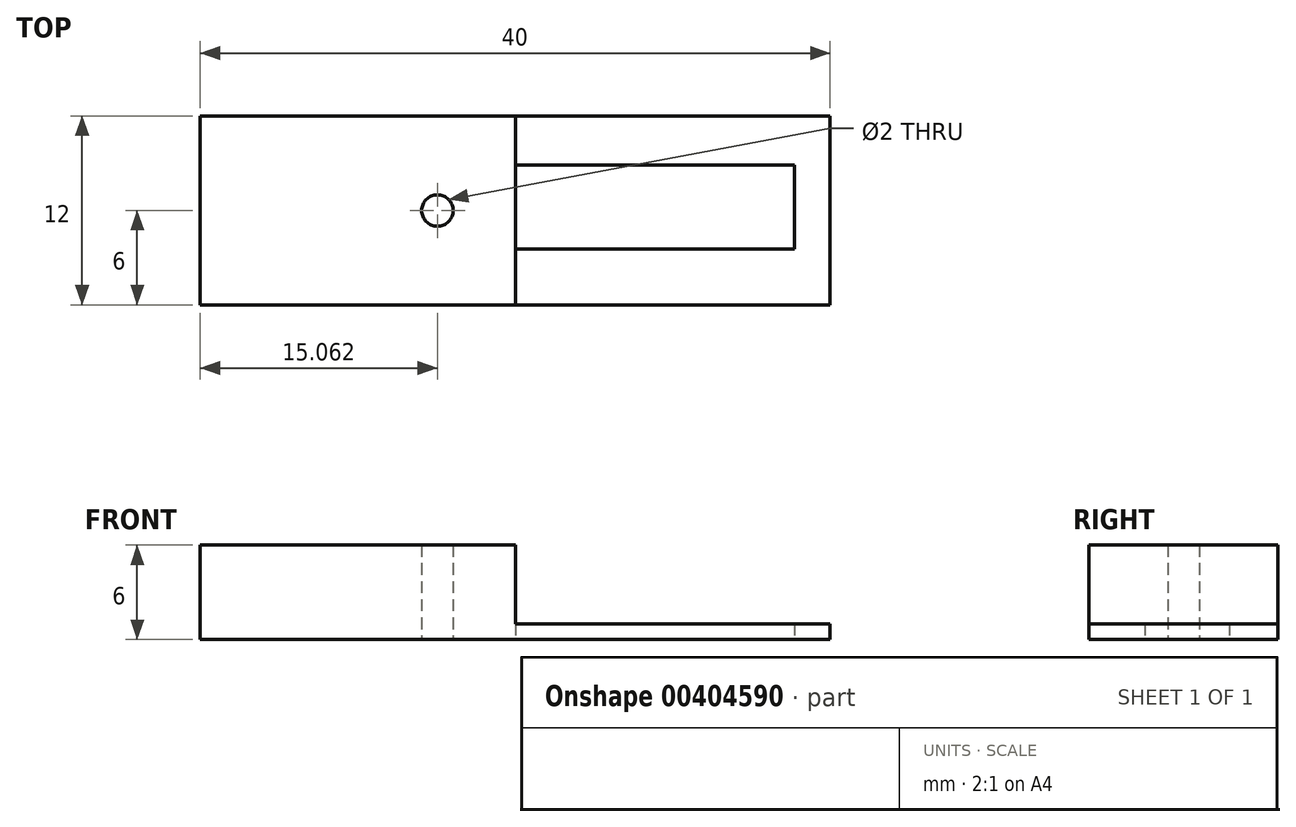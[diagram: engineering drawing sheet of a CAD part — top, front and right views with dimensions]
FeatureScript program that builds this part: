
annotation { "Feature Type Name" : "Feature", "Feature Type Description" : "" }
export const myFeature = defineFeature(function(context is Context, id is Id, definition is map)
    precondition{}
    {
        {
            var Q0;
            Q0=qCreatedBy(makeId("Top.planeOp"),FACE);
            var sketch = newSketch(context, id + "F0", { "sketchPlane" : qUnion([Q0])});
            skLineSegment(sketch, "E0.bottom", {"start": v(0, 0) * mm, "end": v(-40, 0) * mm});
            skLineSegment(sketch, "E0.top", {"start": v(0, 12) * mm, "end": v(-40, 12) * mm});
            skLineSegment(sketch, "E0.left", {"start": v(0, 0) * mm, "end": v(0, 12) * mm});
            skLineSegment(sketch, "E0.right", {"start": v(-40, 0) * mm, "end": v(-40, 12) * mm});
            skLineSegment(sketch, "E1", {"start": v(-40, 6) * mm, "end": v(-25, 6) * mm});
            skLineSegment(sketch, "E2", {"start": v(-24.94, 12) * mm, "end": v(-24.94, 6) * mm});
            skLineSegment(sketch, "E3", {"start": v(-25, 6) * mm, "end": v(-24.94, 6) * mm});
            skCircle(sketch, "E4", {"center": v(-24.94, 6) * mm, "radius": 1 * mm});
            skLineSegment(sketch, "E5", {"start": v(-40, 6) * mm, "end": v(-19.97, 6) * mm});
            skLineSegment(sketch, "E6", {"start": v(-40, 3.56) * mm, "end": v(-19.97, 3.56) * mm});
            skLineSegment(sketch, "E7.bottom", {"start": v(-19.97, 3.56) * mm, "end": v(-2.25, 3.56) * mm});
            skLineSegment(sketch, "E7.top", {"start": v(-19.97, 8.9) * mm, "end": v(-2.25, 8.9) * mm});
            skLineSegment(sketch, "E7.left", {"start": v(-19.97, 3.56) * mm, "end": v(-19.97, 8.9) * mm});
            skLineSegment(sketch, "E7.right", {"start": v(-2.25, 3.56) * mm, "end": v(-2.25, 8.9) * mm});
            skLineSegment(sketch, "E8", {"start": v(-19.97, 8.9) * mm, "end": v(-19.97, 12) * mm});
            skLineSegment(sketch, "E9", {"start": v(-19.97, 12) * mm, "end": v(-19.97, 0) * mm});
            skLineSegment(sketch, "E10", {"start": v(-24.94, 6) * mm, "end": v(-25, 0) * mm});
            skSolve(sketch);
        }
        {
            var Q0;
            {var subQ9=sQuery(id+"F0.wireOp",EDGE,"E0.bottom");Q0=makeQuery(id+"F0.imprint","IMPRINT",FACE,{"disambiguationData":[TD([[makeQuery(id+"F0.imprint","IMPRINT",EDGE,{"derivedFrom":subQ9}),-1.0]])]});}
            var Q1;
            {var subQ8=sQuery(id+"F0.wireOp",EDGE,"E6");Q1=makeQuery(id+"F0.imprint","IMPRINT",FACE,{"disambiguationData":[TD([[makeQuery(id+"F0.imprint","IMPRINT",EDGE,{"derivedFrom":subQ8}),1.0]])]});}
            var Q2;
            {var subQ5=sQuery(id+"F0.wireOp",EDGE,"E0.right");var subQ6=sQuery(id+"F0.wireOp",EDGE,"E0.top");var subQ7=makeQuery(id+"F0.imprint","INTERSECT",VERTEX,{"derivedFrom":[subQ6,subQ5]});Q2=makeQuery(id+"F0.imprint","IMPRINT",FACE,{"disambiguationData":[TD([[makeQuery(id+"F0.imprint","IMPRINT",EDGE,{"disambiguationData":[TD([[subQ7,1.0]])],"derivedFrom":subQ6}),1.0]])]});}
            var Q3;
            {var subQ5=sQuery(id+"F0.wireOp",EDGE,"E2");var subQ8=sQuery(id+"F0.wireOp",EDGE,"E0.top");var subQ10=makeQuery(id+"F0.imprint","INTERSECT",VERTEX,{"derivedFrom":[subQ8,subQ5]});Q3=makeQuery(id+"F0.imprint","IMPRINT",FACE,{"disambiguationData":[TD([[makeQuery(id+"F0.imprint","IMPRINT",EDGE,{"disambiguationData":[TD([[subQ10,1.0]])],"derivedFrom":subQ8}),1.0]])]});}
            extrude(context, id + "F1", {"entities" : qUnion([Q0, Q1, Q2, Q3]), "depth" : 6 * mm});
        }
        {
            var Q0;
            {var subQ1=sQuery(id+"F0.wireOp",EDGE,"E0.left");Q0=makeQuery(id+"F0.imprint","IMPRINT",FACE,{"disambiguationData":[TD([[makeQuery(id+"F0.imprint","IMPRINT",EDGE,{"derivedFrom":subQ1}),1.0]])]});}
            extrude(context, id + "F2", {"entities" : qUnion([Q0]), "operationType" : NewBodyOperationType.ADD, "depth" : 1 * mm});
        }
    });
